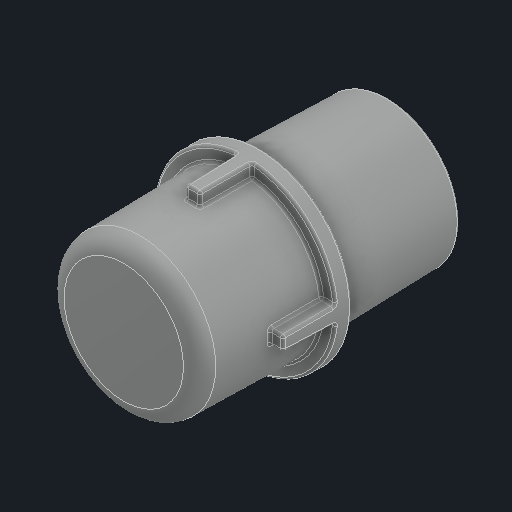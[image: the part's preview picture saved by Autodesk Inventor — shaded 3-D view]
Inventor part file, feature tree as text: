
AUTODESK INVENTOR PART (.ipt)
format: ipt  version: 2025 (Build 290162000, 162)  size: 359,424 bytes
history: native  units: in
note: dims shown in document units (in); Inventor stores cm internally (conversion verified against a paired STEP export)
features: fillet x1
ambient origin geometry x8: Origin, YZ Plane, XZ Plane, XY Plane, X Axis, Y Axis, Z Axis, Center Point
bodies: Solid1 (feature_tree)
feature tree (1):
  fillet  "Fillet3"  [1 undecoded]
note: 1 required parameter value undecoded (feature->parameter linkage not recoverable at this tier; creation-order binding heuristic only, values carry confidence <= 0.55)
